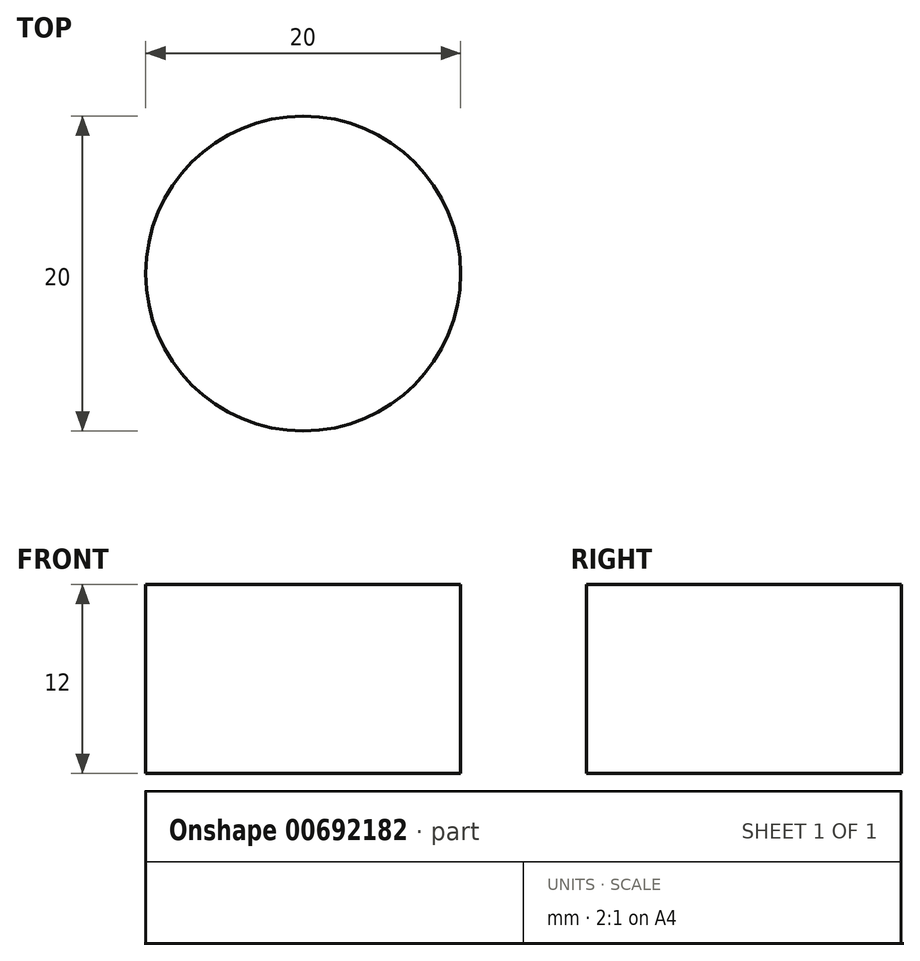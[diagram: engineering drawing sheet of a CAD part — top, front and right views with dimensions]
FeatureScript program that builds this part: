
annotation { "Feature Type Name" : "Feature", "Feature Type Description" : "" }
export const myFeature = defineFeature(function(context is Context, id is Id, definition is map)
    precondition{}
    {
        {
            var Q0;
            Q0=qCreatedBy(makeId("Top.planeOp"),FACE);
            var sketch = newSketch(context, id + "F0", { "sketchPlane" : qUnion([Q0])});
            skCircle(sketch, "E0", {"center": v(0, 0) * mm, "radius": 10 * mm});
            skSolve(sketch);
        }
        {
            var Q0;
            Q0=makeQuery(id+"F0.imprint","IMPRINT",FACE,{"disambiguationData":[TD([[makeQuery(id+"F0.imprint","IMPRINT",EDGE,{"derivedFrom":sQuery(id+"F0.wireOp",EDGE,"E0")}),1.0]])]});
            extrude(context, id + "F1", {"entities" : qUnion([Q0]), "depth" : 12 * mm, "offsetDistance" : 25 * mm});
        }
    });
